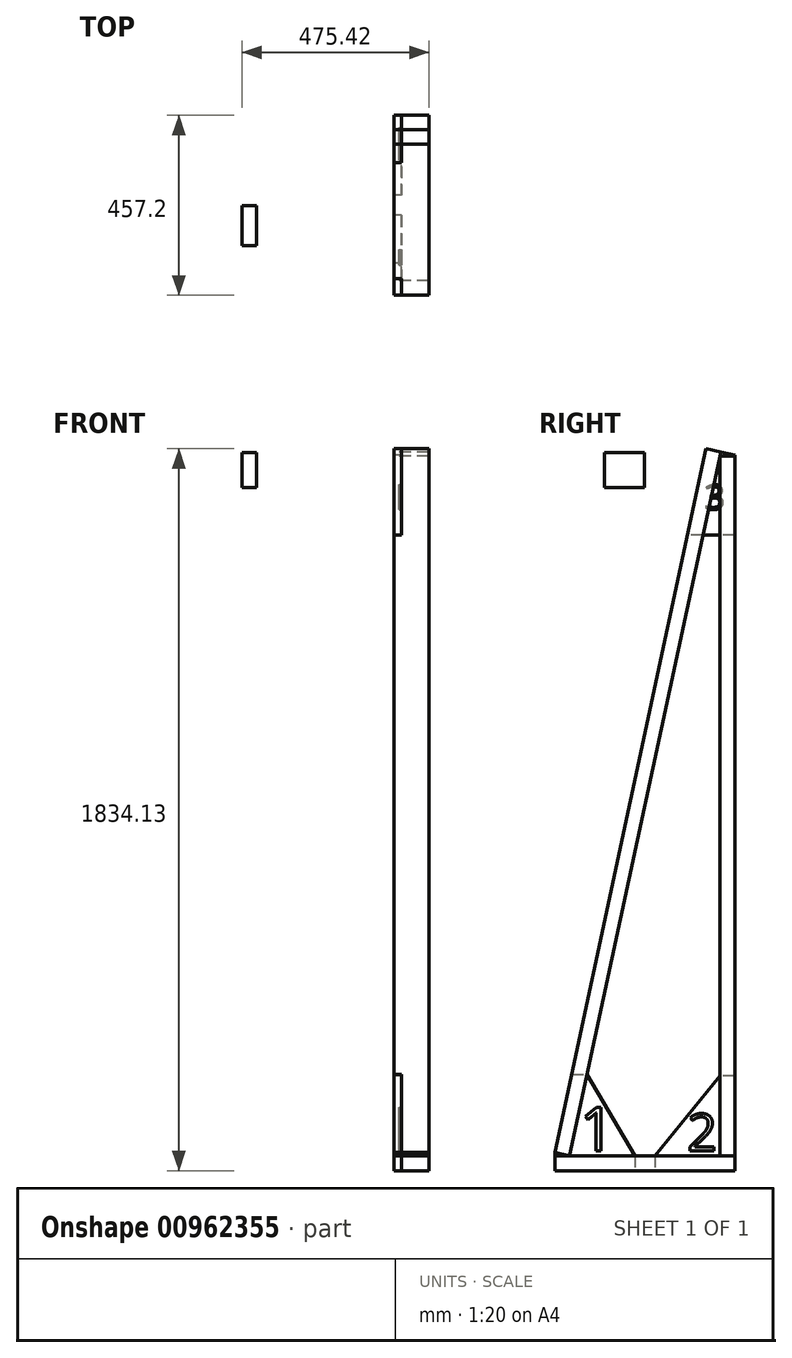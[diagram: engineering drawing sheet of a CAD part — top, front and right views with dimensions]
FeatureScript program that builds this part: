
annotation { "Feature Type Name" : "Feature", "Feature Type Description" : "" }
export const myFeature = defineFeature(function(context is Context, id is Id, definition is map)
    precondition{}
    {
        {
            var Q0;
            Q0=qCreatedBy(makeId("Right.planeOp"),FACE);
            var sketch = newSketch(context, id + "F0", { "sketchPlane" : qUnion([Q0])});
            skLineSegment(sketch, "E0.bottom", {"start": v(-227.88, -2.41) * mm, "end": v(229.32, -2.41) * mm});
            skLineSegment(sketch, "E0.top", {"start": v(-227.88, -40.51) * mm, "end": v(229.32, -40.51) * mm});
            skLineSegment(sketch, "E0.left", {"start": v(-227.88, -2.41) * mm, "end": v(-227.88, -40.51) * mm});
            skLineSegment(sketch, "E0.right", {"start": v(229.32, -2.41) * mm, "end": v(229.32, -40.51) * mm});
            skSolve(sketch);
        }
        {
            var Q0;
            Q0=makeQuery(id+"F0.imprint","IMPRINT",FACE,{"disambiguationData":[TD([[makeQuery(id+"F0.imprint","IMPRINT",EDGE,{"derivedFrom":sQuery(id+"F0.wireOp",EDGE,"E0.bottom")}),-1.0]])]});
            extrude(context, id + "F1", {"entities" : qUnion([Q0]), "depth" : 88.9 * mm, "offsetDistance" : 25.4 * mm});
        }
        {
            var Q0;
            Q0=qCreatedBy(makeId("Right.planeOp"),FACE);
            var sketch = newSketch(context, id + "F2", { "sketchPlane" : qUnion([Q0])});
            skLineSegment(sketch, "E1.bottom", {"start": v(191.22, 1775.59) * mm, "end": v(229.32, 1775.59) * mm});
            skLineSegment(sketch, "E1.top", {"start": v(191.22, -2.41) * mm, "end": v(229.32, -2.41) * mm});
            skLineSegment(sketch, "E1.left", {"start": v(191.22, 1775.59) * mm, "end": v(191.22, -2.41) * mm});
            skLineSegment(sketch, "E1.right", {"start": v(229.32, 1775.59) * mm, "end": v(229.32, -2.41) * mm});
            skSolve(sketch);
        }
        {
            var Q0;
            Q0=makeQuery(id+"F2.imprint","IMPRINT",FACE,{"disambiguationData":[TD([[makeQuery(id+"F2.imprint","IMPRINT",EDGE,{"derivedFrom":sQuery(id+"F2.wireOp",EDGE,"E1.bottom")}),-1.0]])]});
            extrude(context, id + "F3", {"entities" : qUnion([Q0]), "depth" : 88.9 * mm, "offsetDistance" : 25.4 * mm});
        }
        {
            var Q0;
            Q0=qCreatedBy(makeId("Right.planeOp"),FACE);
            var sketch = newSketch(context, id + "F4", { "sketchPlane" : qUnion([Q0])});
            skLineSegment(sketch, "E2", {"start": v(193.37, 1785.62) * mm, "end": v(156.12, 1793.62) * mm});
            skLineSegment(sketch, "E3", {"start": v(156.12, 1793.62) * mm, "end": v(-227.88, 5.59) * mm});
            skLineSegment(sketch, "E4", {"start": v(-227.88, 5.59) * mm, "end": v(-190.63, -2.41) * mm});
            skLineSegment(sketch, "E5", {"start": v(-190.63, -2.41) * mm, "end": v(193.37, 1785.62) * mm});
            skSolve(sketch);
        }
        {
            var Q0;
            Q0=makeQuery(id+"F4.imprint","IMPRINT",FACE,{"disambiguationData":[TD([[makeQuery(id+"F4.imprint","IMPRINT",EDGE,{"derivedFrom":sQuery(id+"F4.wireOp",EDGE,"E2")}),1.0]])]});
            extrude(context, id + "F5", {"entities" : qUnion([Q0]), "depth" : 88.9 * mm, "offsetDistance" : 25.4 * mm});
        }
        {
            var Q0;
            Q0=qCreatedBy(makeId("Right.planeOp"),FACE);
            var sketch = newSketch(context, id + "F6", { "sketchPlane" : qUnion([Q0])});
            skLineSegment(sketch, "E6", {"start": v(229.32, -40.51) * mm, "end": v(229.32, 200.79) * mm});
            skLineSegment(sketch, "E7", {"start": v(229.32, 200.79) * mm, "end": v(191.22, 200.79) * mm});
            skLineSegment(sketch, "E8", {"start": v(191.22, 200.79) * mm, "end": v(26.12, -2.41) * mm});
            skLineSegment(sketch, "E9", {"start": v(26.12, -2.41) * mm, "end": v(26.12, -40.51) * mm});
            skLineSegment(sketch, "E10", {"start": v(26.12, -40.51) * mm, "end": v(229.32, -40.51) * mm});
            skSolve(sketch);
        }
        {
            var Q0;
            Q0=makeQuery(id+"F6.imprint","IMPRINT",FACE,{"disambiguationData":[TD([[makeQuery(id+"F6.imprint","IMPRINT",EDGE,{"derivedFrom":sQuery(id+"F6.wireOp",EDGE,"E6")}),1.0]])]});
            extrude(context, id + "F7", {"entities" : qUnion([Q0]), "depth" : 19.05 * mm, "offsetDistance" : 25.4 * mm});
        }
        {
            var Q0;
            Q0=makeQuery(id+"F7.opExtrude","CAP_FACE",FACE,{"disambiguationData":[OSD([sQuery(id+"F6.wireOp",EDGE,"E6"),sQuery(id+"F6.wireOp",EDGE,"E7"),sQuery(id+"F6.wireOp",EDGE,"E8"),sQuery(id+"F6.wireOp",EDGE,"E9"),sQuery(id+"F6.wireOp",EDGE,"E10")])],"isStart":false});
            var sketch = newSketch(context, id + "F8", { "sketchPlane" : qUnion([Q0])});
            skText(sketch, "E11", { "text": "2", "fontName": "OpenSans-Regular.ttf"});
            const initialGuessF8  = {"E11": [0.10867, 0.01029, 1, 0, 0.09411]};
            skSetInitialGuess(sketch, initialGuessF8);
            skSolve(sketch);
        }
        {
            var Q0;
            Q0=makeQuery(id+"F8.imprint","IMPRINT",FACE,{"disambiguationData":[TD([[makeQuery(id+"F8.imprint","IMPRINT",EDGE,{"derivedFrom":sQuery(id+"F8.wireOp",EDGE,"E11.sketch_text.stroke-0")}),-1.0]])]});
            extrude(context, id + "F9", {"entities" : qUnion([Q0]), "operationType" : NewBodyOperationType.REMOVE, "oppositeDirection" : true, "depth" : 6.35 * mm, "offsetDistance" : 25.4 * mm});
        }
        {
            var Q0;
            Q0=qCreatedBy(makeId("Right.planeOp"),FACE);
            var sketch = newSketch(context, id + "F10", { "sketchPlane" : qUnion([Q0])});
            skLineSegment(sketch, "E12", {"start": v(-227.88, -40.51) * mm, "end": v(-227.88, 5.59) * mm});
            skLineSegment(sketch, "E13", {"start": v(-227.88, 5.59) * mm, "end": v(-185.21, 204.26) * mm});
            skLineSegment(sketch, "E14", {"start": v(-185.21, 204.26) * mm, "end": v(-146.25, 204.26) * mm});
            skLineSegment(sketch, "E15", {"start": v(-146.25, 204.26) * mm, "end": v(-24.68, -2.41) * mm});
            skLineSegment(sketch, "E16", {"start": v(-24.68, -2.41) * mm, "end": v(-24.68, -40.51) * mm});
            skLineSegment(sketch, "E17", {"start": v(-24.68, -40.51) * mm, "end": v(-227.88, -40.51) * mm});
            skSolve(sketch);
        }
        {
            var Q0;
            Q0=makeQuery(id+"F10.imprint","IMPRINT",FACE,{"disambiguationData":[TD([[makeQuery(id+"F10.imprint","IMPRINT",EDGE,{"derivedFrom":sQuery(id+"F10.wireOp",EDGE,"E12")}),-1.0]])]});
            extrude(context, id + "F11", {"entities" : qUnion([Q0]), "depth" : 19.05 * mm, "offsetDistance" : 25.4 * mm});
        }
        {
            var Q0;
            Q0=makeQuery(id+"F11.opExtrude","CAP_FACE",FACE,{"disambiguationData":[OSD([sQuery(id+"F10.wireOp",EDGE,"E12"),sQuery(id+"F10.wireOp",EDGE,"E13"),sQuery(id+"F10.wireOp",EDGE,"E14"),sQuery(id+"F10.wireOp",EDGE,"E15"),sQuery(id+"F10.wireOp",EDGE,"E16"),sQuery(id+"F10.wireOp",EDGE,"E17")])],"isStart":false});
            var sketch = newSketch(context, id + "F12", { "sketchPlane" : qUnion([Q0])});
            skText(sketch, "E18", { "text": "1", "fontName": "OpenSans-Regular.ttf"});
            skPoint(sketch, "E18.firstSnap0", {"position": v(-206.55, 104.92) * mm});
            const initialGuessF12  = {"E18": [-0.16487, 0.01029, 1, 0, 0.11046]};
            skSetInitialGuess(sketch, initialGuessF12);
            skSolve(sketch);
        }
        {
            var Q0;
            Q0 = qSketchRegion(id + "F12", true);
            extrude(context, id + "F13", {"entities" : qUnion([Q0]), "operationType" : NewBodyOperationType.REMOVE, "oppositeDirection" : true, "depth" : 6.35 * mm, "offsetDistance" : 25.4 * mm});
        }
        {
            var Q0;
            Q0=qCreatedBy(makeId("Right.planeOp"),FACE);
            var sketch = newSketch(context, id + "F14", { "sketchPlane" : qUnion([Q0])});
            skLineSegment(sketch, "E19", {"start": v(109.1, 1574.7) * mm, "end": v(156.12, 1793.62) * mm});
            skLineSegment(sketch, "E20", {"start": v(156.12, 1793.62) * mm, "end": v(229.32, 1777.9) * mm});
            skLineSegment(sketch, "E21", {"start": v(229.32, 1777.9) * mm, "end": v(229.32, 1574.7) * mm});
            skLineSegment(sketch, "E22", {"start": v(229.32, 1574.7) * mm, "end": v(109.1, 1574.7) * mm});
            skSolve(sketch);
        }
        {
            var Q0;
            Q0 = qSketchRegion(id + "F14", true);
            extrude(context, id + "F15", {"entities" : qUnion([Q0]), "depth" : 19.05 * mm, "offsetDistance" : 25.4 * mm});
        }
        {
            var Q0;
            Q0=makeQuery(id+"F15.opExtrude","CAP_FACE",FACE,{"disambiguationData":[OSD([sQuery(id+"F14.wireOp",EDGE,"E19"),sQuery(id+"F14.wireOp",EDGE,"E20"),sQuery(id+"F14.wireOp",EDGE,"E21"),sQuery(id+"F14.wireOp",EDGE,"E22")])],"isStart":false});
            var sketch = newSketch(context, id + "F16", { "sketchPlane" : qUnion([Q0])});
            skText(sketch, "E23", { "text": "3\n", "fontName": "OpenSans-Regular.ttf"});
            const initialGuessF16  = {"E23": [0.15312, 1.63955, 1, 0, 0.06328]};
            skSetInitialGuess(sketch, initialGuessF16);
            skSolve(sketch);
        }
        {
            var Q0;
            Q0 = qSketchRegion(id + "F16", true);
            extrude(context, id + "F17", {"entities" : qUnion([Q0]), "operationType" : NewBodyOperationType.REMOVE, "oppositeDirection" : true, "depth" : 6.35 * mm, "offsetDistance" : 25.4 * mm});
        }
        {
            var Q0;
            Q0=qCreatedBy(makeId("Front.planeOp"),FACE);
            var sketch = newSketch(context, id + "F18", { "sketchPlane" : qUnion([Q0])});
            skLineSegment(sketch, "E24.bottom", {"start": v(-386.52, 1784.46) * mm, "end": v(-348.42, 1784.46) * mm});
            skLineSegment(sketch, "E24.top", {"start": v(-386.52, 1695.56) * mm, "end": v(-348.42, 1695.56) * mm});
            skLineSegment(sketch, "E24.left", {"start": v(-386.52, 1784.46) * mm, "end": v(-386.52, 1695.56) * mm});
            skLineSegment(sketch, "E24.right", {"start": v(-348.42, 1784.46) * mm, "end": v(-348.42, 1695.56) * mm});
            skSolve(sketch);
        }
        {
            var Q0;
            Q0 = qSketchRegion(id + "F18", true);
            extrude(context, id + "F19", {"entities" : qUnion([Q0]), "depth" : 101.6 * mm, "offsetDistance" : 25.4 * mm});
        }
    });
